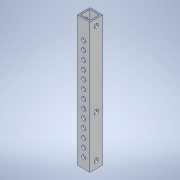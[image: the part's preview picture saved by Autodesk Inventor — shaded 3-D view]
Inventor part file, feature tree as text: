
AUTODESK INVENTOR PART (.ipt)
format: ipt  version: 2020.3 (Build 243373000, 373)  size: 175,104 bytes
history: native  units: mm
features: sketch x5, hole x4, other x1, extrude x1
ambient origin geometry x8: Origin, YZ Plane, XZ Plane, XY Plane, X Axis, Y Axis, Z Axis, Center Point
bodies: Body1 (feature_tree)
feature tree (11):
  other  "ソリッド1"
  extrude  "押し出し1"  Depth=9.0mm
  hole  "穴1"  [1 undecoded]
  hole  "穴4"  [1 undecoded]
  hole  "穴5"  [1 undecoded]
  hole  "穴6"  [1 undecoded]
  sketch  "スケッチ1"
  sketch  "スケッチ2"
  sketch  "スケッチ5"
  sketch  "スケッチ6"
  sketch  "スケッチ7"
note: 4 required parameter values undecoded (feature->parameter linkage not recoverable at this tier; creation-order binding heuristic only, values carry confidence <= 0.55)
